# Revit family: Trane_TVR_Indoor_2-way Cassette_4TVG0007(09,12,15)EF000AA(2nd DC)
name_source: partatom
category: Equipamento mecânico
units: mm (PartAtom-declared; Revit-internal decimal feet)

## family parameters
Com base no plano de trabalho = Não
Compartilhado = Não
Corte com vazios quando carregada = Não
Cota do conector redondo = Utilizar diâmetro
Número OmniClass = 23.75.00.00
Ponto de cálculo do ambiente = Não
Sempre na vertical = Sim
Tipo de parte = Normal
Título OmniClass = Climate Control (HVAC)

## types (4) — shared parameters
Condensation = air
Depth = 591  [stored 1.93898 ft]
Descrição = High efficiency air cooled
Drain pipe = 32  [stored 0.104987 ft]
Fabricante = Trane
Gas = R410a
Gas pipe = 12.7  [stored 0.0416667 ft]
Height = 299
Installation = Indoor installation
Liquid pipe = 6.35  [stored 0.0208333 ft]
Machine material = grilles：ABS/HIPS
Maximum Fuse Amps = 15.000 A
Panel color = SB2014
Power supply = 220-240V, 50/60Hz
Width = 1172  [stored 3.84514 ft]
clearance access behind = 1500
clearance access front = 1500
clearance access left = 100  [stored 0.328084 ft]
clearance access right = 100  [stored 0.328084 ft]

## per-type parameters (varying)
| type | Air Flow | Cooling Capacity | Cooling Power Input | Heating Capacity | Heating Power Input | Minimum Circuit Amps | Net Weight | Series | URL |
| 4TVG0007EF000AA | 654/612/571/530/488/449/410m3/h | 2 kW | 35 W | 3 kW | 35 W | 0.470 A | 33.50 kg | TVR ULTRA | https://www.trane.com |
| 4TVG0009EF000AA | 654/612/571/530/488/449/410m3/h | 3 kW | 40 W | 3 kW | 40 W | 0.470 A | 33.50 kg | TVR ULTRA | https://www.trane.com |
| 4TVG0012EF000AA | 725/679/641/591/554/509/458m3/h | 4 kW | 40 W | 4 kW | 40 W | 0.520 A | 33.50 kg | TVR ULTRA | https://www.trane.com |
| 4TVG0015EF000AA | 850/792/731/670/631/592/550m3/h | 5 kW | 50 W | 5 kW | 50 W | 0.590 A | 35.00 kg | TVR |  |

note: column(s) folded — value = type name in every type: Modelo

note: [stored X ft] marks values corroborated as IEEE doubles in the binary element streams (Revit-internal decimal feet)

## geometry (parser evidence)
native form markers: Blend x2, Sweep x1
no freeform markers — native parametric forms only
